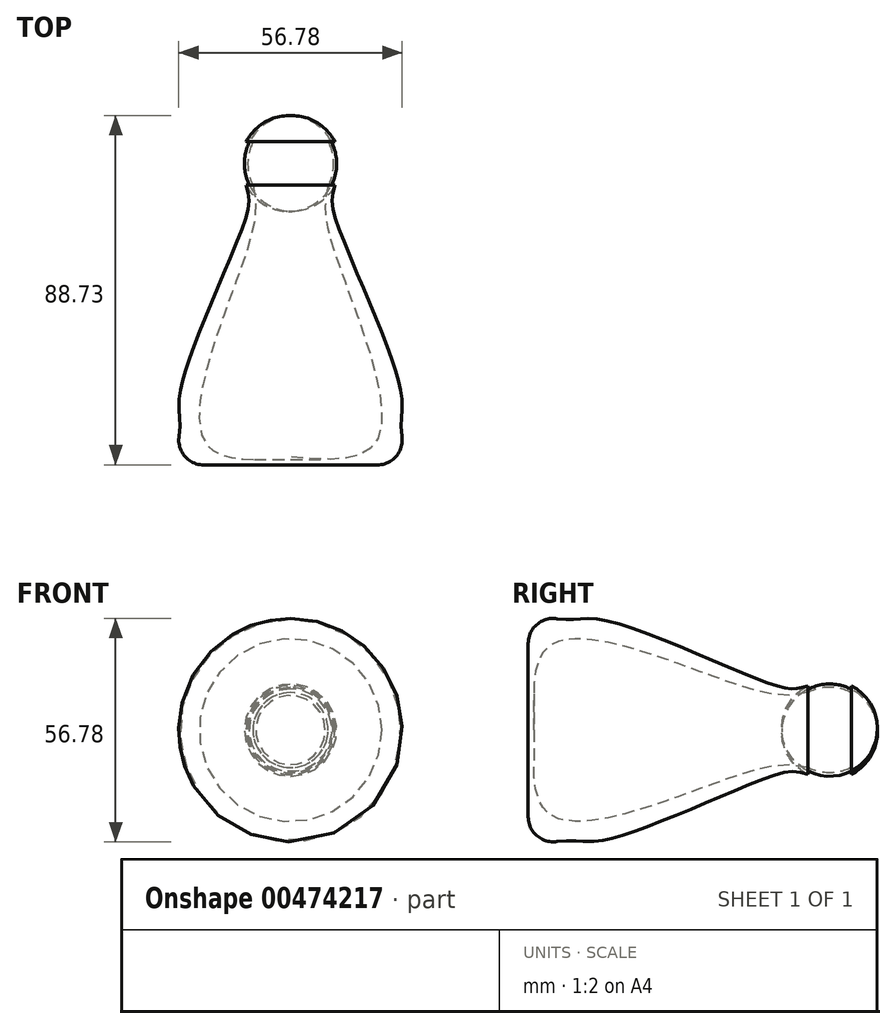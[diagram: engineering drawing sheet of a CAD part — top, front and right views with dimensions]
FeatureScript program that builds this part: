
annotation { "Feature Type Name" : "Feature", "Feature Type Description" : "" }
export const myFeature = defineFeature(function(context is Context, id is Id, definition is map)
    precondition{}
    {
        {
            var Q0;
            Q0=qCreatedBy(makeId("Top.planeOp"),FACE);
            var sketch = newSketch(context, id + "F0", { "sketchPlane" : qUnion([Q0])});
            skArc(sketch, "E0", {"start": v(11.27, 15.05) * mm, "mid": v(12.6, 20.55) * mm, "end": v(11.27, 26.06) * mm});
            skFitSpline(sketch, "E1", {"points": [v(11.27, 15.05) * mm, v(11.27, 7.03) * mm, v(28.06, -37.54) * mm, v(30.68, -56.02) * mm], "startDerivative": vector(-12.03, -41.13) * mm, "endDerivative": vector(44.13, -101.1) * mm});
            skLineSegment(sketch, "E2", {"start": v(22.04, -56.02) * mm, "end": v(0, -56.02) * mm});
            skLineSegment(sketch, "E3", {"start": v(0, 28.06) * mm, "end": v(0, -56.02) * mm});
            skArc(sketch, "E4.filletArc", {"start": v(22.04, -56.02) * mm, "mid": v(26.88, -53.79) * mm, "end": v(28.3, -48.65) * mm});
            skLineSegment(sketch, "E5", {"start": v(0, 47.4) * mm, "end": v(0, -69.01) * mm});
            skLineSegment(sketch, "E6", {"start": v(11.27, 26.06) * mm, "end": v(9.53, 26.06) * mm});
            skArc(sketch, "E7", {"start": v(9.53, 14.93) * mm, "mid": v(10.86, 20.5) * mm, "end": v(9.53, 26.06) * mm});
            skFitSpline(sketch, "E8", {"points": [v(9.53, 14.93) * mm, v(9.53, 3.98) * mm, v(17.23, -18.86) * mm, v(22.04, -49.67) * mm, v(0, -54.04) * mm], "startDerivative": vector(-17.4, -62.1) * mm, "endDerivative": vector(-127.84, 13.33) * mm});
            skSolve(sketch);
        }
        {
            var Q0;
            Q0=makeQuery(id+"F0.imprint","IMPRINT",FACE,{"disambiguationData":[TD([[makeQuery(id+"F0.imprint","IMPRINT",EDGE,{"derivedFrom":sQuery(id+"F0.wireOp",EDGE,"E0")}),1.0]])]});
            var Q1;
            Q1=sQuery(id+"F0.wireOp",EDGE,"E5");
            revolve(context, id + "F1", {"entities" : qUnion([Q0]), "axis" : qUnion([Q1]), "revolveType" : RevolveType.FULL});
        }
    });
